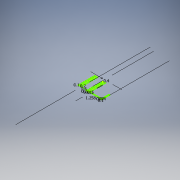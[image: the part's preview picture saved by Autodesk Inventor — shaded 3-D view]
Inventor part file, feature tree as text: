
AUTODESK INVENTOR PART (.ipt)
format: ipt  version: 2019.4 (Build 234330000, 330)  size: 144,896 bytes
history: native  units: in
note: dims shown in document units (in); Inventor stores cm internally (conversion verified against a paired STEP export)
features: sketch x1
ambient origin geometry x8: Origin, YZ Plane, XZ Plane, XY Plane, X Axis, Y Axis, Z Axis, Center Point
feature tree (1):
  sketch  "Sketch1"  dims[d0=0.0157in d1=0.0039in d2=3.937in d4=0.0079in d5=0.3937in d7=0.3937in d9=0.0028in d10=0.0055in d11=0.0006in d12=3.937in d14=0.0039in d15=0.3937in d17=0.3937in d20=0.0495in d21=0.0039in d22=3.937in d24=0.0079in d25=0.3937in d27=0.3937in d29=0.0236in]
